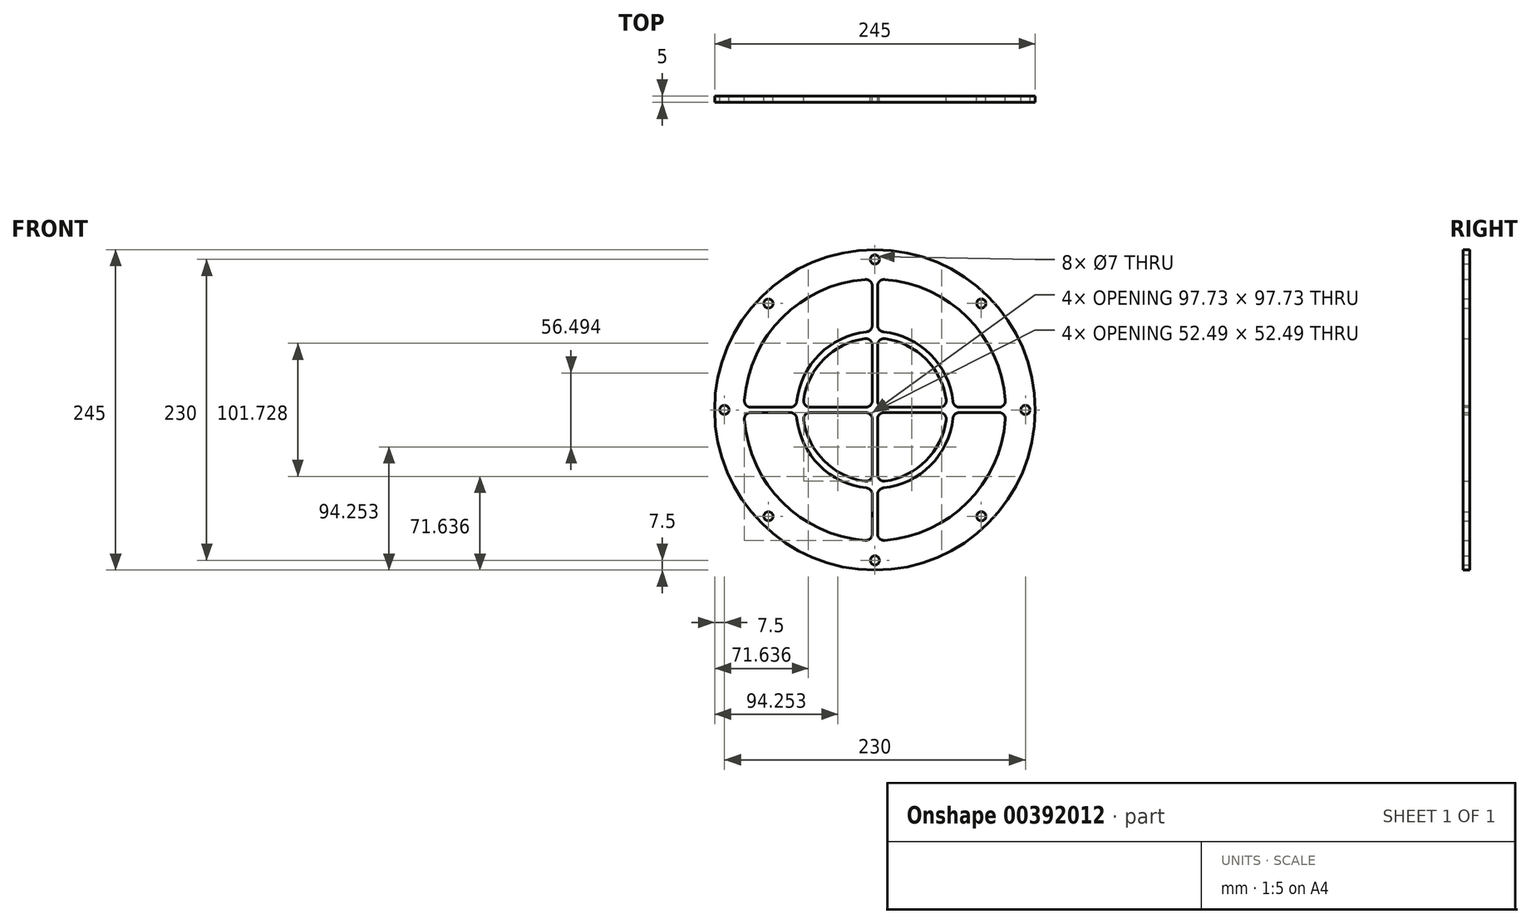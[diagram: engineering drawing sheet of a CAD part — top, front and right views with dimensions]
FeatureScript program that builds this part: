
annotation { "Feature Type Name" : "Feature", "Feature Type Description" : "" }
export const myFeature = defineFeature(function(context is Context, id is Id, definition is map)
    precondition{}
    {
        {
            var Q0;
            Q0=qCreatedBy(makeId("Front.planeOp"),FACE);
            var sketch = newSketch(context, id + "F0", { "sketchPlane" : qUnion([Q0])});
            skCircle(sketch, "E0", {"center": v(0, 0) * mm, "radius": 122.5 * mm});
            skArc(sketch, "E1", {"start": v(-7.37, 99.73) * mm, "mid": v(-70.71, 70.71) * mm, "end": v(-99.73, 7.37) * mm});
            skCircle(sketch, "E2", {"center": v(0, 0) * mm, "radius": 115 * mm, "construction": true});
            skCircle(sketch, "E3", {"center": v(-115, 0) * mm, "radius": 3.5 * mm});
            skCircle(sketch, "E4.1.0", {"center": v(-81.32, -81.32) * mm, "radius": 3.5 * mm});
            skCircle(sketch, "E4.2.0", {"center": v(0, -115) * mm, "radius": 3.5 * mm});
            skCircle(sketch, "E4.3.0", {"center": v(81.32, -81.32) * mm, "radius": 3.5 * mm});
            skCircle(sketch, "E4.4.0", {"center": v(115, 0) * mm, "radius": 3.5 * mm});
            skCircle(sketch, "E4.5.0", {"center": v(81.32, 81.32) * mm, "radius": 3.5 * mm});
            skLineSegment(sketch, "E5.left", {"start": v(2, 94.74) * mm, "end": v(2, 64.62) * mm});
            skLineSegment(sketch, "E5.right", {"start": v(-2, 94.74) * mm, "end": v(-2, 64.62) * mm});
            skLineSegment(sketch, "E6.bottom", {"start": v(-94.74, 2) * mm, "end": v(-64.62, 2) * mm});
            skLineSegment(sketch, "E6.top", {"start": v(-94.74, -2) * mm, "end": v(-64.62, -2) * mm});
            skPoint(sketch, "E7.orphan", {"position": v(-2, 105.37) * mm});
            skPoint(sketch, "E8.orphan", {"position": v(2, 105.37) * mm});
            skPoint(sketch, "E6.left.end.orphan", {"position": v(-105.96, -2) * mm});
            skPoint(sketch, "E6.left.start.orphan", {"position": v(-105.96, 2) * mm});
            skPoint(sketch, "E6.right.start.orphan", {"position": v(105.96, 2) * mm});
            skPoint(sketch, "E9.orphan", {"position": v(105.96, -2) * mm});
            skPoint(sketch, "E5.top.end.orphan", {"position": v(-2, -105.37) * mm});
            skPoint(sketch, "E5.top.start.orphan", {"position": v(2, -105.37) * mm});
            skPoint(sketch, "E10.visualSharp", {"position": v(-2, 99.98) * mm});
            skArc(sketch, "E10.filletArc", {"start": v(-2, 94.74) * mm, "mid": v(-3.6, 98.4) * mm, "end": v(-7.37, 99.73) * mm});
            skPoint(sketch, "E11.visualSharp", {"position": v(2, 99.98) * mm});
            skArc(sketch, "E11.filletArc", {"start": v(7.37, 99.73) * mm, "mid": v(3.6, 98.4) * mm, "end": v(2, 94.74) * mm});
            skArc(sketch, "E12.trimOffspring", {"start": v(-99.73, -7.37) * mm, "mid": v(-70.71, -70.71) * mm, "end": v(-7.37, -99.73) * mm});
            skLineSegment(sketch, "E13.trimOffspring", {"start": v(-2, -7) * mm, "end": v(-2, -49.5) * mm});
            skLineSegment(sketch, "E14.trimOffspring", {"start": v(2, -7) * mm, "end": v(2, -49.5) * mm});
            skLineSegment(sketch, "E15.trimOffspring", {"start": v(7, 2) * mm, "end": v(49.5, 2) * mm});
            skLineSegment(sketch, "E16.trimOffspring", {"start": v(7, -2) * mm, "end": v(49.5, -2) * mm});
            skArc(sketch, "E17.trimOffspring", {"start": v(99.73, 7.37) * mm, "mid": v(70.71, 70.71) * mm, "end": v(7.37, 99.73) * mm});
            skArc(sketch, "E18.trimOffspring", {"start": v(7.37, -99.73) * mm, "mid": v(70.71, -70.71) * mm, "end": v(99.73, -7.37) * mm});
            skPoint(sketch, "E19.visualSharp", {"position": v(-99.98, 2) * mm});
            skArc(sketch, "E19.filletArc", {"start": v(-99.73, 7.37) * mm, "mid": v(-98.4, 3.6) * mm, "end": v(-94.74, 2) * mm});
            skPoint(sketch, "E20.visualSharp", {"position": v(-99.98, -2) * mm});
            skArc(sketch, "E20.filletArc", {"start": v(-94.74, -2) * mm, "mid": v(-98.4, -3.6) * mm, "end": v(-99.73, -7.37) * mm});
            skPoint(sketch, "E21.visualSharp", {"position": v(-2, -2) * mm});
            skArc(sketch, "E21.filletArc", {"start": v(-2, -7) * mm, "mid": v(-3.46, -3.46) * mm, "end": v(-7, -2) * mm});
            skPoint(sketch, "E22.visualSharp", {"position": v(-2, 2) * mm});
            skArc(sketch, "E22.filletArc", {"start": v(-7, 2) * mm, "mid": v(-3.46, 3.46) * mm, "end": v(-2, 7) * mm});
            skPoint(sketch, "E23.visualSharp", {"position": v(2, 2) * mm});
            skArc(sketch, "E23.filletArc", {"start": v(2, 7) * mm, "mid": v(3.46, 3.46) * mm, "end": v(7, 2) * mm});
            skPoint(sketch, "E24.visualSharp", {"position": v(2, -2) * mm});
            skArc(sketch, "E24.filletArc", {"start": v(7, -2) * mm, "mid": v(3.46, -3.46) * mm, "end": v(2, -7) * mm});
            skPoint(sketch, "E25.visualSharp", {"position": v(99.98, -2) * mm});
            skArc(sketch, "E25.filletArc", {"start": v(99.73, -7.37) * mm, "mid": v(98.4, -3.6) * mm, "end": v(94.74, -2) * mm});
            skPoint(sketch, "E26.visualSharp", {"position": v(99.98, 2) * mm});
            skArc(sketch, "E26.filletArc", {"start": v(94.74, 2) * mm, "mid": v(98.4, 3.6) * mm, "end": v(99.73, 7.37) * mm});
            skPoint(sketch, "E27.visualSharp", {"position": v(2, -99.98) * mm});
            skArc(sketch, "E27.filletArc", {"start": v(2, -94.74) * mm, "mid": v(3.6, -98.4) * mm, "end": v(7.37, -99.73) * mm});
            skPoint(sketch, "E28.visualSharp", {"position": v(-2, -99.98) * mm});
            skArc(sketch, "E28.filletArc", {"start": v(-7.37, -99.73) * mm, "mid": v(-3.6, -98.4) * mm, "end": v(-2, -94.74) * mm});
            skArc(sketch, "E29", {"start": v(-6.46, 59.65) * mm, "mid": v(-42.43, 42.43) * mm, "end": v(-59.65, 6.46) * mm});
            skArc(sketch, "E30", {"start": v(-7.7, 54.46) * mm, "mid": v(-38.9, 38.9) * mm, "end": v(-54.46, 7.7) * mm});
            skCircle(sketch, "E31.1.6.0", {"center": v(0, 115) * mm, "radius": 3.5 * mm});
            skCircle(sketch, "E31.1.7.0", {"center": v(-81.32, 81.32) * mm, "radius": 3.5 * mm});
            skLineSegment(sketch, "E32.trimOffspring", {"start": v(-2, 49.5) * mm, "end": v(-2, 7) * mm});
            skLineSegment(sketch, "E33.trimOffspring", {"start": v(2, 49.5) * mm, "end": v(2, 7) * mm});
            skLineSegment(sketch, "E34.trimOffspring", {"start": v(64.62, 2) * mm, "end": v(94.74, 2) * mm});
            skArc(sketch, "E35.trimOffspring", {"start": v(54.46, 7.7) * mm, "mid": v(38.9, 38.9) * mm, "end": v(7.7, 54.46) * mm});
            skLineSegment(sketch, "E36.trimOffspring", {"start": v(64.62, -2) * mm, "end": v(94.74, -2) * mm});
            skArc(sketch, "E37.trimOffspring", {"start": v(59.65, 6.46) * mm, "mid": v(42.43, 42.43) * mm, "end": v(6.46, 59.65) * mm});
            skArc(sketch, "E38.trimOffspring", {"start": v(6.46, -59.65) * mm, "mid": v(42.43, -42.43) * mm, "end": v(59.65, -6.46) * mm});
            skLineSegment(sketch, "E39.trimOffspring", {"start": v(-2, -64.62) * mm, "end": v(-2, -94.74) * mm});
            skArc(sketch, "E40.trimOffspring", {"start": v(7.7, -54.46) * mm, "mid": v(38.9, -38.9) * mm, "end": v(54.46, -7.7) * mm});
            skLineSegment(sketch, "E41.trimOffspring", {"start": v(2, -64.62) * mm, "end": v(2, -94.74) * mm});
            skArc(sketch, "E42.trimOffspring", {"start": v(-59.65, -6.46) * mm, "mid": v(-42.43, -42.43) * mm, "end": v(-6.46, -59.65) * mm});
            skLineSegment(sketch, "E43.trimOffspring", {"start": v(-49.5, 2) * mm, "end": v(-7, 2) * mm});
            skLineSegment(sketch, "E44.trimOffspring", {"start": v(-49.5, -2) * mm, "end": v(-7, -2) * mm});
            skArc(sketch, "E45.trimOffspring", {"start": v(-54.46, -7.7) * mm, "mid": v(-38.9, -38.9) * mm, "end": v(-7.7, -54.46) * mm});
            skPoint(sketch, "E46.visualSharp", {"position": v(-2, 59.97) * mm});
            skArc(sketch, "E46.filletArc", {"start": v(-6.46, 59.65) * mm, "mid": v(-3.28, 61.28) * mm, "end": v(-2, 64.62) * mm});
            skPoint(sketch, "E47.visualSharp", {"position": v(-2, 54.96) * mm});
            skArc(sketch, "E47.filletArc", {"start": v(-2, 49.5) * mm, "mid": v(-3.72, 53.28) * mm, "end": v(-7.7, 54.46) * mm});
            skPoint(sketch, "E48.visualSharp", {"position": v(2, 59.97) * mm});
            skArc(sketch, "E48.filletArc", {"start": v(2, 64.62) * mm, "mid": v(3.28, 61.28) * mm, "end": v(6.46, 59.65) * mm});
            skPoint(sketch, "E49.visualSharp", {"position": v(2, 54.96) * mm});
            skArc(sketch, "E49.filletArc", {"start": v(7.7, 54.46) * mm, "mid": v(3.72, 53.28) * mm, "end": v(2, 49.5) * mm});
            skPoint(sketch, "E50.visualSharp", {"position": v(-59.97, 2) * mm});
            skArc(sketch, "E50.filletArc", {"start": v(-64.62, 2) * mm, "mid": v(-61.28, 3.28) * mm, "end": v(-59.65, 6.46) * mm});
            skPoint(sketch, "E51.visualSharp", {"position": v(-54.96, 2) * mm});
            skArc(sketch, "E51.filletArc", {"start": v(-54.46, 7.7) * mm, "mid": v(-53.28, 3.72) * mm, "end": v(-49.5, 2) * mm});
            skPoint(sketch, "E52.visualSharp", {"position": v(-54.96, -2) * mm});
            skArc(sketch, "E52.filletArc", {"start": v(-49.5, -2) * mm, "mid": v(-53.28, -3.72) * mm, "end": v(-54.46, -7.7) * mm});
            skPoint(sketch, "E53.visualSharp", {"position": v(-59.97, -2) * mm});
            skArc(sketch, "E53.filletArc", {"start": v(-59.65, -6.46) * mm, "mid": v(-61.28, -3.28) * mm, "end": v(-64.62, -2) * mm});
            skPoint(sketch, "E54.visualSharp", {"position": v(54.96, -2) * mm});
            skArc(sketch, "E54.filletArc", {"start": v(54.46, -7.7) * mm, "mid": v(53.28, -3.72) * mm, "end": v(49.5, -2) * mm});
            skPoint(sketch, "E55.visualSharp", {"position": v(59.97, -2) * mm});
            skArc(sketch, "E55.filletArc", {"start": v(64.62, -2) * mm, "mid": v(61.28, -3.28) * mm, "end": v(59.65, -6.46) * mm});
            skPoint(sketch, "E56.visualSharp", {"position": v(59.97, 2) * mm});
            skArc(sketch, "E56.filletArc", {"start": v(59.65, 6.46) * mm, "mid": v(61.28, 3.28) * mm, "end": v(64.62, 2) * mm});
            skPoint(sketch, "E57.visualSharp", {"position": v(54.96, 2) * mm});
            skArc(sketch, "E57.filletArc", {"start": v(49.5, 2) * mm, "mid": v(53.28, 3.72) * mm, "end": v(54.46, 7.7) * mm});
            skPoint(sketch, "E58.visualSharp", {"position": v(2, -59.97) * mm});
            skArc(sketch, "E58.filletArc", {"start": v(6.46, -59.65) * mm, "mid": v(3.28, -61.28) * mm, "end": v(2, -64.62) * mm});
            skPoint(sketch, "E59.visualSharp", {"position": v(2, -54.96) * mm});
            skArc(sketch, "E59.filletArc", {"start": v(2, -49.5) * mm, "mid": v(3.72, -53.28) * mm, "end": v(7.7, -54.46) * mm});
            skPoint(sketch, "E60.visualSharp", {"position": v(-2, -54.96) * mm});
            skArc(sketch, "E60.filletArc", {"start": v(-7.7, -54.46) * mm, "mid": v(-3.72, -53.28) * mm, "end": v(-2, -49.5) * mm});
            skPoint(sketch, "E61.visualSharp", {"position": v(-2, -59.97) * mm});
            skArc(sketch, "E61.filletArc", {"start": v(-2, -64.62) * mm, "mid": v(-3.28, -61.28) * mm, "end": v(-6.46, -59.65) * mm});
            skSolve(sketch);
        }
        {
            var Q0;
            Q0=makeQuery(id+"F0.imprint","IMPRINT",FACE,{"disambiguationData":[TD([[makeQuery(id+"F0.imprint","IMPRINT",EDGE,{"derivedFrom":sQuery(id+"F0.wireOp",EDGE,"E0")}),1.0]])]});
            var Q1;
            {var subQ0=sQuery(id+"F0.wireOp",EDGE,"E29");var subQ1=sQuery(id+"F0.wireOp",EDGE,"E6.bottom");var subQ2=makeQuery(id+"F0.imprint","INTERSECT",VERTEX,{"derivedFrom":[subQ1,subQ0]});Q1=makeQuery(id+"F0.imprint","IMPRINT",FACE,{"disambiguationData":[TD([[makeQuery(id+"F0.imprint","IMPRINT",EDGE,{"disambiguationData":[TD([[subQ2,-1.0]])],"derivedFrom":subQ1}),-1.0]])]});}
            var Q2;
            {var subQ0=sQuery(id+"F0.wireOp",EDGE,"E30");var subQ1=sQuery(id+"F0.wireOp",EDGE,"E15.trimOffspring");var subQ2=makeQuery(id+"F0.imprint","INTERSECT",VERTEX,{"derivedFrom":[subQ1,subQ0]});Q2=makeQuery(id+"F0.imprint","IMPRINT",FACE,{"disambiguationData":[TD([[makeQuery(id+"F0.imprint","IMPRINT",EDGE,{"disambiguationData":[TD([[subQ2,-1.0]])],"derivedFrom":subQ1}),-1.0]])]});}
            var Q3;
            {var subQ0=sQuery(id+"F0.wireOp",EDGE,"E21.filletArc");Q3=makeQuery(id+"F0.imprint","IMPRINT",FACE,{"disambiguationData":[TD([[makeQuery(id+"F0.imprint","IMPRINT",EDGE,{"derivedFrom":subQ0}),-1.0]])]});}
            var Q4;
            {var subQ0=sQuery(id+"F0.wireOp",EDGE,"E30");var subQ1=sQuery(id+"F0.wireOp",EDGE,"E13.trimOffspring");var subQ2=makeQuery(id+"F0.imprint","INTERSECT",VERTEX,{"derivedFrom":[subQ1,subQ0]});Q4=makeQuery(id+"F0.imprint","IMPRINT",FACE,{"disambiguationData":[TD([[makeQuery(id+"F0.imprint","IMPRINT",EDGE,{"disambiguationData":[TD([[subQ2,-1.0]])],"derivedFrom":subQ1}),1.0]])]});}
            var Q5;
            {var subQ0=sQuery(id+"F0.wireOp",EDGE,"E29");var subQ1=sQuery(id+"F0.wireOp",EDGE,"E5.left");var subQ2=makeQuery(id+"F0.imprint","INTERSECT",VERTEX,{"derivedFrom":[subQ1,subQ0]});Q5=makeQuery(id+"F0.imprint","IMPRINT",FACE,{"disambiguationData":[TD([[makeQuery(id+"F0.imprint","IMPRINT",EDGE,{"disambiguationData":[TD([[subQ2,-1.0]])],"derivedFrom":subQ1}),-1.0]])]});}
            extrude(context, id + "F1", {"entities" : qUnion([Q0, Q1, Q2, Q3, Q4, Q5]), "depth" : 5 * mm});
        }
    });
